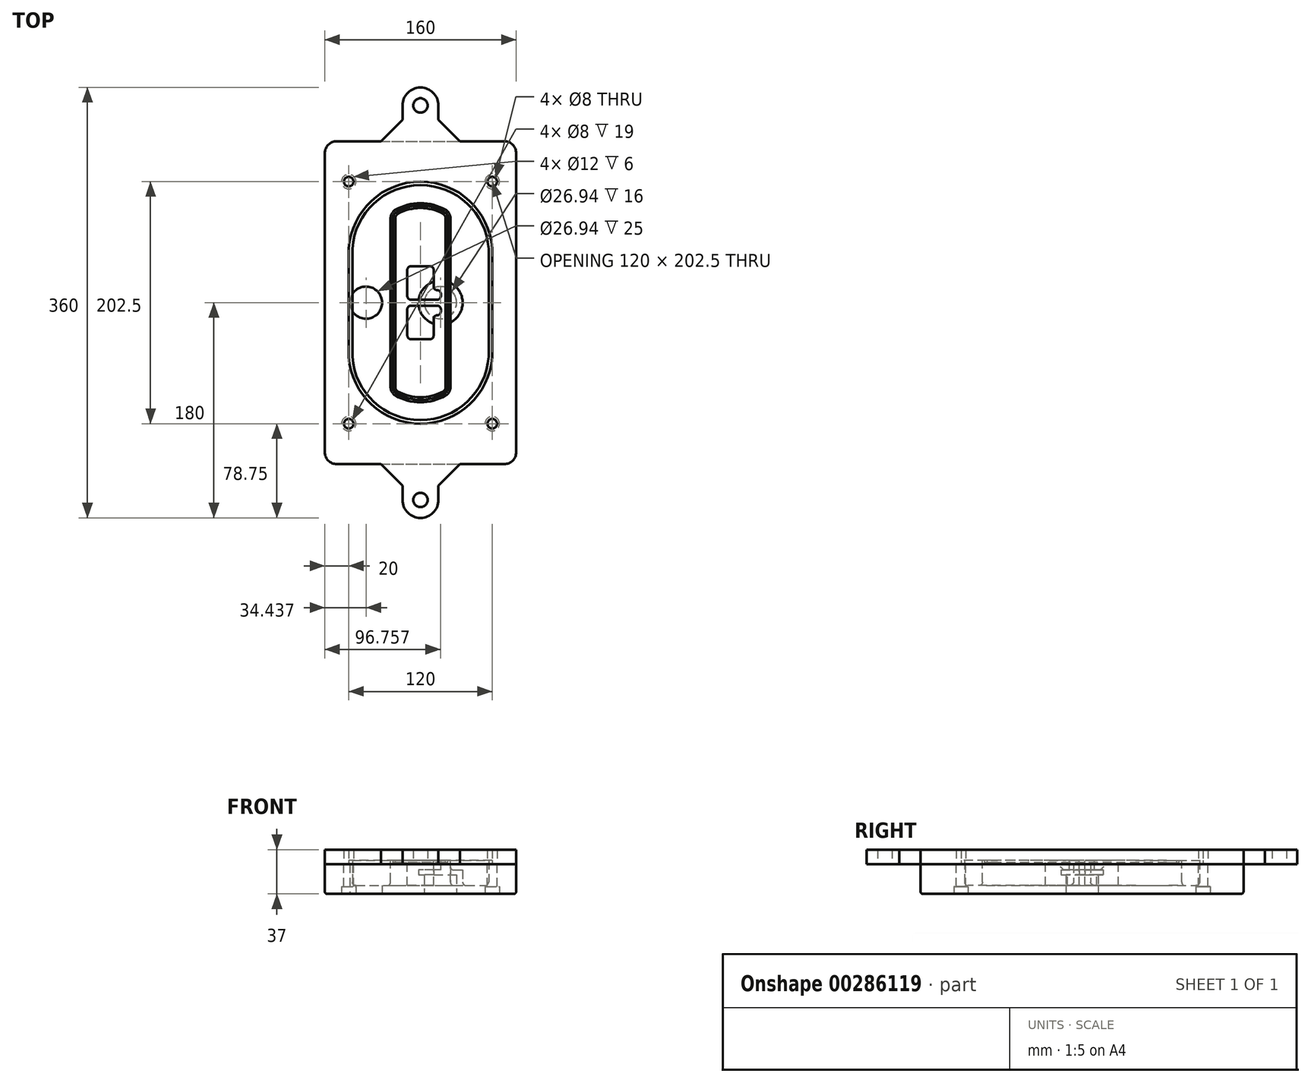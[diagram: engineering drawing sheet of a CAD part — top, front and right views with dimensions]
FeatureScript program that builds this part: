
annotation { "Feature Type Name" : "Feature", "Feature Type Description" : "" }
export const myFeature = defineFeature(function(context is Context, id is Id, definition is map)
    precondition{}
    {
        {
            var Q0;
            Q0=qCreatedBy(makeId("Top.planeOp"),FACE);
            var sketch = newSketch(context, id + "F0", { "sketchPlane" : qUnion([Q0])});
            skPoint(sketch, "E0.rect.middle", {"position": v(0, 0) * mm});
            skLineSegment(sketch, "E1.bottom", {"start": v(-70, -135) * mm, "end": v(70, -135) * mm});
            skLineSegment(sketch, "E1.top", {"start": v(-70, 135) * mm, "end": v(70, 135) * mm});
            skLineSegment(sketch, "E1.left", {"start": v(-80, -125) * mm, "end": v(-80, 125) * mm});
            skLineSegment(sketch, "E1.right", {"start": v(80, -125) * mm, "end": v(80, 125) * mm});
            skLineSegment(sketch, "E2", {"start": v(-80, 135) * mm, "end": v(80, -135) * mm, "construction": true});
            skLineSegment(sketch, "E3", {"start": v(80, 135) * mm, "end": v(-80, -135) * mm, "construction": true});
            skCircle(sketch, "E4", {"center": v(-60, 101.25) * mm, "radius": 4 * mm});
            skCircle(sketch, "E5", {"center": v(60, 101.25) * mm, "radius": 4 * mm});
            skCircle(sketch, "E6", {"center": v(60, -101.25) * mm, "radius": 4 * mm});
            skCircle(sketch, "E7", {"center": v(-60, -101.25) * mm, "radius": 4 * mm});
            skLineSegment(sketch, "E8", {"start": v(-60, 101.25) * mm, "end": v(60, 101.25) * mm, "construction": true});
            skLineSegment(sketch, "E9", {"start": v(60, 101.25) * mm, "end": v(60, -101.25) * mm, "construction": true});
            skLineSegment(sketch, "E10", {"start": v(60, -101.25) * mm, "end": v(-60, -101.25) * mm, "construction": true});
            skLineSegment(sketch, "E11", {"start": v(-60, -101.25) * mm, "end": v(-60, 101.25) * mm, "construction": true});
            skLineSegment(sketch, "E12", {"start": v(-60, 44.66) * mm, "end": v(-60, -44.66) * mm});
            skLineSegment(sketch, "E13", {"start": v(60, 44.66) * mm, "end": v(60, -44.66) * mm});
            skArc(sketch, "E14", {"start": v(59.98, 45.37) * mm, "mid": v(0, 101.25) * mm, "end": v(-59.98, 45.37) * mm});
            skArc(sketch, "E15", {"start": v(-59.98, -45.37) * mm, "mid": v(0, -101.25) * mm, "end": v(59.98, -45.37) * mm});
            skLineSegment(sketch, "E16", {"start": v(-60, 0) * mm, "end": v(60, 0) * mm, "construction": true});
            skPoint(sketch, "E17.visualSharp", {"position": v(-60, -45) * mm});
            skArc(sketch, "E17.filletArc", {"start": v(-60, -44.66) * mm, "mid": v(-60, -45.02) * mm, "end": v(-59.98, -45.37) * mm});
            skPoint(sketch, "E18.visualSharp", {"position": v(-60, 45) * mm});
            skArc(sketch, "E18.filletArc", {"start": v(-59.98, 45.37) * mm, "mid": v(-60, 45.02) * mm, "end": v(-60, 44.66) * mm});
            skPoint(sketch, "E19.visualSharp", {"position": v(60, 45) * mm});
            skArc(sketch, "E19.filletArc", {"start": v(60, 44.66) * mm, "mid": v(60, 45.02) * mm, "end": v(59.98, 45.37) * mm});
            skPoint(sketch, "E20.visualSharp", {"position": v(60, -45) * mm});
            skArc(sketch, "E20.filletArc", {"start": v(59.98, -45.37) * mm, "mid": v(60, -45.02) * mm, "end": v(60, -44.66) * mm});
            skPoint(sketch, "E21.visualSharp", {"position": v(-80, 135) * mm});
            skArc(sketch, "E21.filletArc", {"start": v(-70, 135) * mm, "mid": v(-77.07, 132.07) * mm, "end": v(-80, 125) * mm});
            skPoint(sketch, "E22.visualSharp", {"position": v(80, 135) * mm});
            skArc(sketch, "E22.filletArc", {"start": v(80, 125) * mm, "mid": v(77.07, 132.07) * mm, "end": v(70, 135) * mm});
            skPoint(sketch, "E23.visualSharp", {"position": v(80, -135) * mm});
            skArc(sketch, "E23.filletArc", {"start": v(70, -135) * mm, "mid": v(77.07, -132.07) * mm, "end": v(80, -125) * mm});
            skPoint(sketch, "E24.visualSharp", {"position": v(-80, -135) * mm});
            skArc(sketch, "E24.filletArc", {"start": v(-80, -125) * mm, "mid": v(-77.07, -132.07) * mm, "end": v(-70, -135) * mm});
            skArc(sketch, "E25.0", {"start": v(57, 44.66) * mm, "mid": v(57, 44.9) * mm, "end": v(56.98, 45.16) * mm});
            skLineSegment(sketch, "E25.1", {"start": v(57, 44.66) * mm, "end": v(57, -44.66) * mm});
            skArc(sketch, "E25.2", {"start": v(56.98, -45.16) * mm, "mid": v(57, -44.9) * mm, "end": v(57, -44.66) * mm});
            skArc(sketch, "E25.3", {"start": v(-56.98, -45.16) * mm, "mid": v(0, -98.25) * mm, "end": v(56.98, -45.16) * mm});
            skArc(sketch, "E25.4", {"start": v(-57, -44.66) * mm, "mid": v(-57, -44.9) * mm, "end": v(-56.98, -45.16) * mm});
            skArc(sketch, "E25.5", {"start": v(56.98, 45.16) * mm, "mid": v(0, 98.25) * mm, "end": v(-56.98, 45.16) * mm});
            skLineSegment(sketch, "E25.6", {"start": v(-57, 44.66) * mm, "end": v(-57, -44.66) * mm});
            skArc(sketch, "E25.7", {"start": v(-56.98, 45.16) * mm, "mid": v(-57, 44.9) * mm, "end": v(-57, 44.66) * mm});
            skArc(sketch, "E26.0", {"start": v(-63.97, 45.65) * mm, "mid": v(-64, 45.16) * mm, "end": v(-64, 44.66) * mm});
            skArc(sketch, "E26.1", {"start": v(63.97, 45.65) * mm, "mid": v(0, 105.25) * mm, "end": v(-63.97, 45.65) * mm});
            skArc(sketch, "E26.2", {"start": v(64, 44.66) * mm, "mid": v(64, 45.16) * mm, "end": v(63.97, 45.65) * mm});
            skLineSegment(sketch, "E26.3", {"start": v(64, 44.66) * mm, "end": v(64, -44.66) * mm});
            skArc(sketch, "E26.4", {"start": v(63.97, -45.65) * mm, "mid": v(64, -45.16) * mm, "end": v(64, -44.66) * mm});
            skLineSegment(sketch, "E26.5", {"start": v(-64, 44.66) * mm, "end": v(-64, -44.66) * mm});
            skArc(sketch, "E26.6", {"start": v(-63.97, -45.65) * mm, "mid": v(0, -105.25) * mm, "end": v(63.97, -45.65) * mm});
            skArc(sketch, "E26.7", {"start": v(-64, -44.66) * mm, "mid": v(-64, -45.16) * mm, "end": v(-63.97, -45.65) * mm});
            skSolve(sketch);
        }
        {
            var Q0;
            Q0=makeQuery(id+"F0.imprint","IMPRINT",FACE,{"disambiguationData":[TD([[makeQuery(id+"F0.imprint","IMPRINT",EDGE,{"derivedFrom":sQuery(id+"F0.wireOp",EDGE,"E1.bottom")}),1.0]])]});
            var Q1;
            Q1=makeQuery(id+"F0.imprint","IMPRINT",FACE,{"disambiguationData":[TD([[makeQuery(id+"F0.imprint","IMPRINT",EDGE,{"derivedFrom":sQuery(id+"F0.wireOp",EDGE,"E12")}),1.0]])]});
            var Q2;
            Q2=makeQuery(id+"F0.imprint","IMPRINT",FACE,{"disambiguationData":[TD([[makeQuery(id+"F0.imprint","IMPRINT",EDGE,{"derivedFrom":sQuery(id+"F0.wireOp",EDGE,"E25.0")}),1.0]])]});
            var Q3;
            Q3=makeQuery(id+"F0.imprint","IMPRINT",FACE,{"disambiguationData":[TD([[makeQuery(id+"F0.imprint","IMPRINT",EDGE,{"derivedFrom":sQuery(id+"F0.wireOp",EDGE,"E12")}),-1.0]])]});
            extrude(context, id + "F1", {"entities" : qUnion([Q0, Q1, Q2, Q3]), "oppositeDirection" : true, "depth" : 25 * mm});
        }
        {
            var Q0;
            Q0=makeQuery(id+"F0.imprint","IMPRINT",FACE,{"disambiguationData":[TD([[makeQuery(id+"F0.imprint","IMPRINT",EDGE,{"derivedFrom":sQuery(id+"F0.wireOp",EDGE,"E12")}),1.0]])]});
            extrude(context, id + "F2", {"entities" : qUnion([Q0]), "operationType" : NewBodyOperationType.ADD, "depth" : 3 * mm});
        }
        {
            var Q0;
            Q0=makeQuery(id+"F0.imprint","IMPRINT",FACE,{"disambiguationData":[TD([[makeQuery(id+"F0.imprint","IMPRINT",EDGE,{"derivedFrom":sQuery(id+"F0.wireOp",EDGE,"E25.0")}),1.0]])]});
            extrude(context, id + "F3", {"entities" : qUnion([Q0]), "operationType" : NewBodyOperationType.REMOVE, "oppositeDirection" : true, "depth" : 18 * mm});
        }
        {
            var Q0;
            Q0=makeQuery(id+"F2.opExtrude","CAP_FACE",FACE,{"disambiguationData":[OSD([sQuery(id+"F0.wireOp",EDGE,"E12"),sQuery(id+"F0.wireOp",EDGE,"E13"),sQuery(id+"F0.wireOp",EDGE,"E14"),sQuery(id+"F0.wireOp",EDGE,"E15"),sQuery(id+"F0.wireOp",EDGE,"E17.filletArc"),sQuery(id+"F0.wireOp",EDGE,"E18.filletArc"),sQuery(id+"F0.wireOp",EDGE,"E19.filletArc"),sQuery(id+"F0.wireOp",EDGE,"E20.filletArc"),sQuery(id+"F0.wireOp",EDGE,"E25.0"),sQuery(id+"F0.wireOp",EDGE,"E25.1"),sQuery(id+"F0.wireOp",EDGE,"E25.2"),sQuery(id+"F0.wireOp",EDGE,"E25.3"),sQuery(id+"F0.wireOp",EDGE,"E25.4"),sQuery(id+"F0.wireOp",EDGE,"E25.5"),sQuery(id+"F0.wireOp",EDGE,"E25.6"),sQuery(id+"F0.wireOp",EDGE,"E25.7")])],"isStart":false});
            var sketch = newSketch(context, id + "F4", { "sketchPlane" : qUnion([Q0])});
            skArc(sketch, "E27.0", {"start": v(-20.99, -77.65) * mm, "mid": v(0, -83.25) * mm, "end": v(20.99, -77.65) * mm});
            skArc(sketch, "E28.0", {"start": v(20.99, 77.65) * mm, "mid": v(0, 83.25) * mm, "end": v(-20.99, 77.65) * mm});
            skLineSegment(sketch, "E29", {"start": v(-25, 70.71) * mm, "end": v(-25, -70.71) * mm});
            skLineSegment(sketch, "E30", {"start": v(25, 70.71) * mm, "end": v(25, -70.71) * mm});
            skLineSegment(sketch, "E31", {"start": v(-25, 75.03) * mm, "end": v(25, 75.03) * mm, "construction": true});
            skLineSegment(sketch, "E32", {"start": v(-25, -75.03) * mm, "end": v(25, -75.03) * mm, "construction": true});
            skPoint(sketch, "E33.visualSharp", {"position": v(-25, 75.03) * mm});
            skArc(sketch, "E33.filletArc", {"start": v(-20.99, 77.65) * mm, "mid": v(-23.92, 74.72) * mm, "end": v(-25, 70.71) * mm});
            skPoint(sketch, "E34.visualSharp", {"position": v(25, 75.03) * mm});
            skArc(sketch, "E34.filletArc", {"start": v(25, 70.71) * mm, "mid": v(23.92, 74.72) * mm, "end": v(20.99, 77.65) * mm});
            skPoint(sketch, "E35.visualSharp", {"position": v(25, -75.03) * mm});
            skArc(sketch, "E35.filletArc", {"start": v(20.99, -77.65) * mm, "mid": v(23.92, -74.72) * mm, "end": v(25, -70.71) * mm});
            skPoint(sketch, "E36.visualSharp", {"position": v(-25, -75.03) * mm});
            skArc(sketch, "E36.filletArc", {"start": v(-25, -70.71) * mm, "mid": v(-23.92, -74.72) * mm, "end": v(-20.99, -77.65) * mm});
            skArc(sketch, "E37.0", {"start": v(56.98, 45.16) * mm, "mid": v(0, 98.25) * mm, "end": v(-56.98, 45.16) * mm});
            skArc(sketch, "E37.1", {"start": v(-56.98, 45.16) * mm, "mid": v(-57, 44.9) * mm, "end": v(-57, 44.66) * mm});
            skLineSegment(sketch, "E37.2", {"start": v(-57, 44.66) * mm, "end": v(-57, -44.66) * mm});
            skArc(sketch, "E37.3", {"start": v(-57, -44.66) * mm, "mid": v(-57, -44.9) * mm, "end": v(-56.98, -45.16) * mm});
            skArc(sketch, "E37.4", {"start": v(-56.98, -45.16) * mm, "mid": v(0, -98.25) * mm, "end": v(56.98, -45.16) * mm});
            skArc(sketch, "E37.5", {"start": v(56.98, -45.16) * mm, "mid": v(57, -44.9) * mm, "end": v(57, -44.66) * mm});
            skLineSegment(sketch, "E37.6", {"start": v(57, 44.66) * mm, "end": v(57, -44.66) * mm});
            skArc(sketch, "E37.7", {"start": v(57, 44.66) * mm, "mid": v(57, 44.9) * mm, "end": v(56.98, 45.16) * mm});
            skLineSegment(sketch, "E38.0", {"start": v(23, 70.71) * mm, "end": v(23, -70.71) * mm});
            skArc(sketch, "E38.1", {"start": v(19.99, -75.92) * mm, "mid": v(22.2, -73.72) * mm, "end": v(23, -70.71) * mm});
            skArc(sketch, "E38.2", {"start": v(-19.99, -75.92) * mm, "mid": v(0, -81.25) * mm, "end": v(19.99, -75.92) * mm});
            skArc(sketch, "E38.3", {"start": v(-23, -70.71) * mm, "mid": v(-22.2, -73.72) * mm, "end": v(-19.99, -75.92) * mm});
            skLineSegment(sketch, "E38.4", {"start": v(-23, 70.71) * mm, "end": v(-23, -70.71) * mm});
            skArc(sketch, "E38.5", {"start": v(23, 70.71) * mm, "mid": v(22.2, 73.72) * mm, "end": v(19.99, 75.92) * mm});
            skArc(sketch, "E38.6", {"start": v(-19.99, 75.92) * mm, "mid": v(-22.2, 73.72) * mm, "end": v(-23, 70.71) * mm});
            skArc(sketch, "E38.7", {"start": v(19.99, 75.92) * mm, "mid": v(0, 81.25) * mm, "end": v(-19.99, 75.92) * mm});
            skArc(sketch, "E39.0", {"start": v(21, 70.71) * mm, "mid": v(20.46, 72.72) * mm, "end": v(19, 74.18) * mm});
            skLineSegment(sketch, "E39.1", {"start": v(21, 70.71) * mm, "end": v(21, -70.71) * mm});
            skArc(sketch, "E39.2", {"start": v(19, -74.18) * mm, "mid": v(20.46, -72.72) * mm, "end": v(21, -70.71) * mm});
            skArc(sketch, "E39.3", {"start": v(-19, -74.18) * mm, "mid": v(0, -79.25) * mm, "end": v(19, -74.18) * mm});
            skArc(sketch, "E39.4", {"start": v(-21, -70.71) * mm, "mid": v(-20.46, -72.72) * mm, "end": v(-19, -74.18) * mm});
            skArc(sketch, "E39.5", {"start": v(19, 74.18) * mm, "mid": v(0, 79.25) * mm, "end": v(-19, 74.18) * mm});
            skLineSegment(sketch, "E39.6", {"start": v(-21, 70.71) * mm, "end": v(-21, -70.71) * mm});
            skArc(sketch, "E39.7", {"start": v(-19, 74.18) * mm, "mid": v(-20.46, 72.72) * mm, "end": v(-21, 70.71) * mm});
            skLineSegment(sketch, "E40", {"start": v(-25, 0) * mm, "end": v(25, 0) * mm, "construction": true});
            skLineSegment(sketch, "E41", {"start": v(-11, 5.5) * mm, "end": v(-11, 27.5) * mm});
            skLineSegment(sketch, "E42", {"start": v(-8, 30.5) * mm, "end": v(8, 30.5) * mm});
            skLineSegment(sketch, "E43", {"start": v(11, 27.5) * mm, "end": v(11, 13.5) * mm});
            skLineSegment(sketch, "E44", {"start": v(14, 10.5) * mm, "end": v(14, 10.5) * mm});
            skLineSegment(sketch, "E45", {"start": v(17, 7.5) * mm, "end": v(17, 5.5) * mm});
            skLineSegment(sketch, "E46", {"start": v(14, 2.5) * mm, "end": v(-8, 2.5) * mm});
            skPoint(sketch, "E47.visualSharp", {"position": v(-11, 30.5) * mm});
            skArc(sketch, "E47.filletArc", {"start": v(-8, 30.5) * mm, "mid": v(-10.12, 29.62) * mm, "end": v(-11, 27.5) * mm});
            skPoint(sketch, "E48.visualSharp", {"position": v(11, 30.5) * mm});
            skArc(sketch, "E48.filletArc", {"start": v(11, 27.5) * mm, "mid": v(10.12, 29.62) * mm, "end": v(8, 30.5) * mm});
            skPoint(sketch, "E49.visualSharp", {"position": v(11, 10.5) * mm});
            skArc(sketch, "E49.filletArc", {"start": v(11, 13.5) * mm, "mid": v(11.88, 11.38) * mm, "end": v(14, 10.5) * mm});
            skPoint(sketch, "E50.visualSharp", {"position": v(17, 10.5) * mm});
            skArc(sketch, "E50.filletArc", {"start": v(17, 7.5) * mm, "mid": v(16.12, 9.62) * mm, "end": v(14, 10.5) * mm});
            skPoint(sketch, "E51.visualSharp", {"position": v(17, 2.5) * mm});
            skArc(sketch, "E51.filletArc", {"start": v(14, 2.5) * mm, "mid": v(16.12, 3.38) * mm, "end": v(17, 5.5) * mm});
            skPoint(sketch, "E52.visualSharp", {"position": v(-11, 2.5) * mm});
            skArc(sketch, "E52.filletArc", {"start": v(-11, 5.5) * mm, "mid": v(-10.12, 3.38) * mm, "end": v(-8, 2.5) * mm});
            skLineSegment(sketch, "E53.0.MirrorCS", {"start": v(14, -2.5) * mm, "end": v(-8, -2.5) * mm});
            skArc(sketch, "E54.0.MirrorCS", {"start": v(-11, -5.5) * mm, "mid": v(-10.12, -3.38) * mm, "end": v(-8, -2.5) * mm});
            skLineSegment(sketch, "E55.0.MirrorCS", {"start": v(-11, -5.5) * mm, "end": v(-11, -27.5) * mm});
            skArc(sketch, "E56.0.MirrorCS", {"start": v(-8, -30.5) * mm, "mid": v(-10.12, -29.62) * mm, "end": v(-11, -27.5) * mm});
            skLineSegment(sketch, "E57.0.MirrorCS", {"start": v(-8, -30.5) * mm, "end": v(8, -30.5) * mm});
            skArc(sketch, "E58.0.MirrorCS", {"start": v(11, -27.5) * mm, "mid": v(10.12, -29.62) * mm, "end": v(8, -30.5) * mm});
            skLineSegment(sketch, "E59.0.MirrorCS", {"start": v(11, -27.5) * mm, "end": v(11, -13.5) * mm});
            skArc(sketch, "E60.0.MirrorCS", {"start": v(11, -13.5) * mm, "mid": v(11.88, -11.38) * mm, "end": v(14, -10.5) * mm});
            skArc(sketch, "E61.0.MirrorCS", {"start": v(17, -7.5) * mm, "mid": v(16.12, -9.62) * mm, "end": v(14, -10.5) * mm});
            skLineSegment(sketch, "E62.0.MirrorCS", {"start": v(17, -7.5) * mm, "end": v(17, -5.5) * mm});
            skArc(sketch, "E63.0.MirrorCS", {"start": v(14, -2.5) * mm, "mid": v(16.12, -3.38) * mm, "end": v(17, -5.5) * mm});
            skSolve(sketch);
        }
        {
            var Q0;
            Q0=makeQuery(id+"F4.imprint","IMPRINT",FACE,{"disambiguationData":[TD([[makeQuery(id+"F4.imprint","IMPRINT",EDGE,{"derivedFrom":sQuery(id+"F4.wireOp",EDGE,"E27.0")}),1.0]])]});
            var Q1;
            Q1=makeQuery(id+"F4.imprint","IMPRINT",FACE,{"disambiguationData":[TD([[makeQuery(id+"F4.imprint","IMPRINT",EDGE,{"derivedFrom":sQuery(id+"F4.wireOp",EDGE,"E38.0")}),-1.0]])]});
            var Q2;
            Q2=makeQuery(id+"F4.imprint","IMPRINT",FACE,{"disambiguationData":[TD([[makeQuery(id+"F4.imprint","IMPRINT",EDGE,{"derivedFrom":sQuery(id+"F4.wireOp",EDGE,"E39.0")}),1.0]])]});
            extrude(context, id + "F5", {"entities" : qUnion([Q0, Q1, Q2]), "operationType" : NewBodyOperationType.ADD, "endBound" : BoundingType.UP_TO_NEXT, "oppositeDirection" : true, "depth" : 25 * mm});
        }
        {
            var Q0;
            Q0=makeQuery(id+"F4.imprint","IMPRINT",FACE,{"disambiguationData":[TD([[makeQuery(id+"F4.imprint","IMPRINT",EDGE,{"derivedFrom":sQuery(id+"F4.wireOp",EDGE,"E38.0")}),-1.0]])]});
            extrude(context, id + "F6", {"entities" : qUnion([Q0]), "operationType" : NewBodyOperationType.REMOVE, "oppositeDirection" : true, "depth" : 2 * mm});
        }
        {
            var Q0;
            Q0=makeQuery(id+"F1.opExtrude","CAP_FACE",FACE,{"disambiguationData":[OSD([sQuery(id+"F0.wireOp",EDGE,"E1.bottom"),sQuery(id+"F0.wireOp",EDGE,"E1.top"),sQuery(id+"F0.wireOp",EDGE,"E1.left"),sQuery(id+"F0.wireOp",EDGE,"E1.right"),sQuery(id+"F0.wireOp",EDGE,"E4"),sQuery(id+"F0.wireOp",EDGE,"E5"),sQuery(id+"F0.wireOp",EDGE,"E6"),sQuery(id+"F0.wireOp",EDGE,"E7"),sQuery(id+"F0.wireOp",EDGE,"E21.filletArc"),sQuery(id+"F0.wireOp",EDGE,"E22.filletArc"),sQuery(id+"F0.wireOp",EDGE,"E23.filletArc"),sQuery(id+"F0.wireOp",EDGE,"E24.filletArc")])],"isStart":false});
            var sketch = newSketch(context, id + "F7", { "sketchPlane" : qUnion([Q0])});
            skCircle(sketch, "E64", {"center": v(16.76, 0) * mm, "radius": 13.47 * mm});
            skCircle(sketch, "E65", {"center": v(-45.56, 0) * mm, "radius": 13.47 * mm});
            skLineSegment(sketch, "E66", {"start": v(80, 0) * mm, "end": v(-80, 0) * mm});
            skCircle(sketch, "E67", {"center": v(16.76, 0) * mm, "radius": 18.47 * mm});
            skCircle(sketch, "E68", {"center": v(60, -101.25) * mm, "radius": 6 * mm});
            skCircle(sketch, "E69", {"center": v(-60, -101.25) * mm, "radius": 6 * mm});
            skCircle(sketch, "E70", {"center": v(-60, 101.25) * mm, "radius": 6 * mm});
            skCircle(sketch, "E71", {"center": v(60, 101.25) * mm, "radius": 6 * mm});
            skSolve(sketch);
        }
        {
            var Q0;
            {var subQ1=sQuery(id+"F7.wireOp",EDGE,"E66");var subQ4=sQuery(id+"F7.wireOp",EDGE,"E64");var subQ6=makeQuery(id+"F7.imprint","INTERSECT",VERTEX,{"disambiguationData":[OD(0.0)],"derivedFrom":[subQ4,subQ1]});Q0=makeQuery(id+"F7.imprint","IMPRINT",FACE,{"disambiguationData":[TD([[makeQuery(id+"F7.imprint","IMPRINT",EDGE,{"disambiguationData":[TD([[subQ6,-1.0]])],"derivedFrom":subQ4}),-1.0]])]});}
            var Q1;
            {var subQ0=sQuery(id+"F7.wireOp",EDGE,"E66");var subQ1=sQuery(id+"F7.wireOp",EDGE,"E64");var subQ3=makeQuery(id+"F7.imprint","INTERSECT",VERTEX,{"disambiguationData":[OD(0.0)],"derivedFrom":[subQ1,subQ0]});Q1=makeQuery(id+"F7.imprint","IMPRINT",FACE,{"disambiguationData":[TD([[makeQuery(id+"F7.imprint","IMPRINT",EDGE,{"disambiguationData":[TD([[subQ3,-1.0]])],"derivedFrom":subQ1}),1.0]])]});}
            var Q2;
            {var subQ0=sQuery(id+"F7.wireOp",EDGE,"E66");var subQ1=sQuery(id+"F7.wireOp",EDGE,"E64");var subQ3=makeQuery(id+"F7.imprint","INTERSECT",VERTEX,{"disambiguationData":[OD(0.0)],"derivedFrom":[subQ1,subQ0]});Q2=makeQuery(id+"F7.imprint","IMPRINT",FACE,{"disambiguationData":[TD([[makeQuery(id+"F7.imprint","IMPRINT",EDGE,{"disambiguationData":[TD([[subQ3,1.0]])],"derivedFrom":subQ1}),1.0]])]});}
            var Q3;
            {var subQ1=sQuery(id+"F7.wireOp",EDGE,"E66");var subQ4=sQuery(id+"F7.wireOp",EDGE,"E64");var subQ6=makeQuery(id+"F7.imprint","INTERSECT",VERTEX,{"disambiguationData":[OD(0.0)],"derivedFrom":[subQ4,subQ1]});Q3=makeQuery(id+"F7.imprint","IMPRINT",FACE,{"disambiguationData":[TD([[makeQuery(id+"F7.imprint","IMPRINT",EDGE,{"disambiguationData":[TD([[subQ6,1.0]])],"derivedFrom":subQ4}),-1.0]])]});}
            extrude(context, id + "F8", {"entities" : qUnion([Q0, Q1, Q2, Q3]), "operationType" : NewBodyOperationType.ADD, "oppositeDirection" : true, "depth" : 20 * mm});
        }
        {
            var Q0;
            {var subQ0=sQuery(id+"F7.wireOp",EDGE,"E66");var subQ1=sQuery(id+"F7.wireOp",EDGE,"E64");var subQ3=makeQuery(id+"F7.imprint","INTERSECT",VERTEX,{"disambiguationData":[OD(0.0)],"derivedFrom":[subQ1,subQ0]});Q0=makeQuery(id+"F7.imprint","IMPRINT",FACE,{"disambiguationData":[TD([[makeQuery(id+"F7.imprint","IMPRINT",EDGE,{"disambiguationData":[TD([[subQ3,-1.0]])],"derivedFrom":subQ1}),1.0]])]});}
            var Q1;
            {var subQ0=sQuery(id+"F7.wireOp",EDGE,"E66");var subQ1=sQuery(id+"F7.wireOp",EDGE,"E64");var subQ3=makeQuery(id+"F7.imprint","INTERSECT",VERTEX,{"disambiguationData":[OD(0.0)],"derivedFrom":[subQ1,subQ0]});Q1=makeQuery(id+"F7.imprint","IMPRINT",FACE,{"disambiguationData":[TD([[makeQuery(id+"F7.imprint","IMPRINT",EDGE,{"disambiguationData":[TD([[subQ3,1.0]])],"derivedFrom":subQ1}),1.0]])]});}
            extrude(context, id + "F9", {"entities" : qUnion([Q0, Q1]), "operationType" : NewBodyOperationType.REMOVE, "oppositeDirection" : true, "depth" : 16 * mm});
        }
        {
            var Q0;
            {var subQ0=sQuery(id+"F7.wireOp",EDGE,"E66");var subQ1=sQuery(id+"F7.wireOp",EDGE,"E65");var subQ3=makeQuery(id+"F7.imprint","INTERSECT",VERTEX,{"disambiguationData":[OD(0.0)],"derivedFrom":[subQ1,subQ0]});Q0=makeQuery(id+"F7.imprint","IMPRINT",FACE,{"disambiguationData":[TD([[makeQuery(id+"F7.imprint","IMPRINT",EDGE,{"disambiguationData":[TD([[subQ3,-1.0]])],"derivedFrom":subQ1}),1.0]])]});}
            var Q1;
            {var subQ0=sQuery(id+"F7.wireOp",EDGE,"E66");var subQ1=sQuery(id+"F7.wireOp",EDGE,"E65");var subQ3=makeQuery(id+"F7.imprint","INTERSECT",VERTEX,{"disambiguationData":[OD(0.0)],"derivedFrom":[subQ1,subQ0]});Q1=makeQuery(id+"F7.imprint","IMPRINT",FACE,{"disambiguationData":[TD([[makeQuery(id+"F7.imprint","IMPRINT",EDGE,{"disambiguationData":[TD([[subQ3,1.0]])],"derivedFrom":subQ1}),1.0]])]});}
            extrude(context, id + "F10", {"entities" : qUnion([Q0, Q1]), "operationType" : NewBodyOperationType.REMOVE, "oppositeDirection" : true, "depth" : 25 * mm});
        }
        {
            var Q0;
            Q0=makeQuery(id+"F7.imprint","IMPRINT",FACE,{"disambiguationData":[TD([[makeQuery(id+"F7.imprint","IMPRINT",EDGE,{"derivedFrom":sQuery(id+"F7.wireOp",EDGE,"E68")}),1.0]])]});
            var Q1;
            Q1=makeQuery(id+"F7.imprint","IMPRINT",FACE,{"disambiguationData":[TD([[makeQuery(id+"F7.imprint","IMPRINT",EDGE,{"derivedFrom":makeQuery(id+"F1.opExtrude","CAP_EDGE",EDGE,{"disambiguationData":[OSD([sQuery(id+"F0.wireOp",EDGE,"E5")])],"isStart":false})}),-1.0]])]});
            var Q2;
            Q2=makeQuery(id+"F7.imprint","IMPRINT",FACE,{"disambiguationData":[TD([[makeQuery(id+"F7.imprint","IMPRINT",EDGE,{"derivedFrom":sQuery(id+"F7.wireOp",EDGE,"E69")}),1.0]])]});
            var Q3;
            Q3=makeQuery(id+"F7.imprint","IMPRINT",FACE,{"disambiguationData":[TD([[makeQuery(id+"F7.imprint","IMPRINT",EDGE,{"derivedFrom":makeQuery(id+"F1.opExtrude","CAP_EDGE",EDGE,{"disambiguationData":[OSD([sQuery(id+"F0.wireOp",EDGE,"E4")])],"isStart":false})}),-1.0]])]});
            var Q4;
            Q4=makeQuery(id+"F7.imprint","IMPRINT",FACE,{"disambiguationData":[TD([[makeQuery(id+"F7.imprint","IMPRINT",EDGE,{"derivedFrom":sQuery(id+"F7.wireOp",EDGE,"E70")}),1.0]])]});
            var Q5;
            Q5=makeQuery(id+"F7.imprint","IMPRINT",FACE,{"disambiguationData":[TD([[makeQuery(id+"F7.imprint","IMPRINT",EDGE,{"derivedFrom":makeQuery(id+"F1.opExtrude","CAP_EDGE",EDGE,{"disambiguationData":[OSD([sQuery(id+"F0.wireOp",EDGE,"E7")])],"isStart":false})}),-1.0]])]});
            var Q6;
            Q6=makeQuery(id+"F7.imprint","IMPRINT",FACE,{"disambiguationData":[TD([[makeQuery(id+"F7.imprint","IMPRINT",EDGE,{"derivedFrom":sQuery(id+"F7.wireOp",EDGE,"E71")}),1.0]])]});
            var Q7;
            Q7=makeQuery(id+"F7.imprint","IMPRINT",FACE,{"disambiguationData":[TD([[makeQuery(id+"F7.imprint","IMPRINT",EDGE,{"derivedFrom":makeQuery(id+"F1.opExtrude","CAP_EDGE",EDGE,{"disambiguationData":[OSD([sQuery(id+"F0.wireOp",EDGE,"E6")])],"isStart":false})}),-1.0]])]});
            extrude(context, id + "F11", {"entities" : qUnion([Q0, Q1, Q2, Q3, Q4, Q5, Q6, Q7]), "operationType" : NewBodyOperationType.REMOVE, "oppositeDirection" : true, "depth" : 6 * mm});
        }
        {
            var Q0;
            Q0=makeQuery(id+"F9.boolean.opBoolean","COPY",FACE,{"derivedFrom":makeQuery(id+"F9.opExtrude","CAP_FACE",FACE,{"disambiguationData":[OSD([sQuery(id+"F7.wireOp",EDGE,"E64")])],"isStart":false})});
            var sketch = newSketch(context, id + "F12", { "sketchPlane" : qUnion([Q0])});
            skArc(sketch, "E72.0", {"start": v(11, 17.55) * mm, "mid": v(2.57, 11.82) * mm, "end": v(-1.54, 2.5) * mm});
            skArc(sketch, "E72.1", {"start": v(-1.54, -2.5) * mm, "mid": v(2.57, -11.82) * mm, "end": v(11, -17.55) * mm});
            skLineSegment(sketch, "E73", {"start": v(-1.54, -2.5) * mm, "end": v(14, -2.5) * mm});
            skLineSegment(sketch, "E74.0", {"start": v(14, 2.5) * mm, "end": v(-1.54, 2.5) * mm});
            skArc(sketch, "E74.1", {"start": v(14, 2.5) * mm, "mid": v(16.12, 3.38) * mm, "end": v(17, 5.5) * mm});
            skLineSegment(sketch, "E74.2", {"start": v(17, 7.5) * mm, "end": v(17, 5.5) * mm});
            skArc(sketch, "E74.3", {"start": v(17, 7.5) * mm, "mid": v(16.12, 9.62) * mm, "end": v(14, 10.5) * mm});
            skArc(sketch, "E74.4", {"start": v(11, 13.5) * mm, "mid": v(11.88, 11.38) * mm, "end": v(14, 10.5) * mm});
            skLineSegment(sketch, "E74.5", {"start": v(11, 17.55) * mm, "end": v(11, 13.5) * mm});
            skLineSegment(sketch, "E74.7", {"start": v(14, -2.5) * mm, "end": v(-1.54, -2.5) * mm});
            skArc(sketch, "E74.8", {"start": v(14, -2.5) * mm, "mid": v(16.12, -3.38) * mm, "end": v(17, -5.5) * mm});
            skLineSegment(sketch, "E74.9", {"start": v(17, -7.5) * mm, "end": v(17, -5.5) * mm});
            skArc(sketch, "E74.10", {"start": v(17, -7.5) * mm, "mid": v(16.12, -9.62) * mm, "end": v(14, -10.5) * mm});
            skArc(sketch, "E74.11", {"start": v(11, -13.5) * mm, "mid": v(11.88, -11.38) * mm, "end": v(14, -10.5) * mm});
            skLineSegment(sketch, "E74.12", {"start": v(11, -17.55) * mm, "end": v(11, -13.5) * mm});
            skPoint(sketch, "E75.orphan", {"position": v(11, -27.5) * mm});
            skPoint(sketch, "E76.orphan", {"position": v(-8, -2.5) * mm});
            skPoint(sketch, "E77.orphan", {"position": v(-8, 2.5) * mm});
            skPoint(sketch, "E78.orphan", {"position": v(11, 27.5) * mm});
            skSolve(sketch);
        }
        {
            var Q0;
            {var subQ7=sQuery(id+"F12.wireOp",EDGE,"E72.0");var subQ14=sQuery(id+"F12.wireOp",EDGE,"E72.1");var subQ16=sQuery(id+"F12.wireOp",EDGE,"E74.1");var subQ18=sQuery(id+"F12.wireOp",EDGE,"E74.8");Q0=qUnion([makeQuery(id+"F12.imprint","IMPRINT",FACE,{"disambiguationData":[TD([[makeQuery(id+"F12.imprint","IMPRINT",EDGE,{"derivedFrom":subQ7}),1.0]])]}),makeQuery(id+"F12.imprint","IMPRINT",FACE,{"disambiguationData":[TD([[makeQuery(id+"F12.imprint","IMPRINT",EDGE,{"derivedFrom":subQ14}),1.0]])]}),makeQuery(id+"F12.imprint","IMPRINT",FACE,{"disambiguationData":[TD([[makeQuery(id+"F12.imprint","IMPRINT",EDGE,{"derivedFrom":subQ16}),1.0]])]}),makeQuery(id+"F12.imprint","IMPRINT",FACE,{"disambiguationData":[TD([[makeQuery(id+"F12.imprint","IMPRINT",EDGE,{"derivedFrom":subQ18}),-1.0]])]})]);}
            var Q1;
            Q1=makeQuery(id+"F5.boolean.opBoolean","SPLIT",FACE,{"disambiguationData":[TD([makeQuery(id+"F5.opExtrude","SWEPT_FACE",FACE,{"disambiguationData":[OSD([sQuery(id+"F4.wireOp",EDGE,"E41")])]})])],"derivedFrom":makeQuery(id+"F3.boolean.opBoolean","COPY",FACE,{"derivedFrom":makeQuery(id+"F3.opExtrude","CAP_FACE",FACE,{"disambiguationData":[OSD([sQuery(id+"F0.wireOp",EDGE,"E25.0"),sQuery(id+"F0.wireOp",EDGE,"E25.1"),sQuery(id+"F0.wireOp",EDGE,"E25.2"),sQuery(id+"F0.wireOp",EDGE,"E25.3"),sQuery(id+"F0.wireOp",EDGE,"E25.4"),sQuery(id+"F0.wireOp",EDGE,"E25.5"),sQuery(id+"F0.wireOp",EDGE,"E25.6"),sQuery(id+"F0.wireOp",EDGE,"E25.7")])],"isStart":false})})});
            extrude(context, id + "F13", {"entities" : qUnion([Q0]), "operationType" : NewBodyOperationType.REMOVE, "endBound" : BoundingType.UP_TO_SURFACE, "endBoundEntityFace" : qUnion([Q1]), "depth" : 25 * mm});
        }
        {
            var Q0;
            Q0=makeQuery(id+"F3.boolean.opBoolean","COPY",EDGE,{"derivedFrom":makeQuery(id+"F3.opExtrude","CAP_EDGE",EDGE,{"disambiguationData":[OSD([sQuery(id+"F0.wireOp",EDGE,"E25.6")])],"isStart":false})});
            var Q1;
            Q1=makeQuery(id+"F8.boolean.opBoolean","INTERSECT",EDGE,{"derivedFrom":[makeQuery(id+"F5.opExtrude","SWEPT_FACE",FACE,{"disambiguationData":[OSD([sQuery(id+"F4.wireOp",EDGE,"E30")])]}),makeQuery(id+"F8.opExtrude","CAP_FACE",FACE,{"disambiguationData":[OSD([sQuery(id+"F7.wireOp",EDGE,"E67")])],"isStart":false})]});
            var Q2;
            Q2=makeQuery(id+"F8.boolean.opBoolean","INTERSECT",EDGE,{"disambiguationData":[OD(1.0)],"derivedFrom":[makeQuery(id+"F5.opExtrude","SWEPT_FACE",FACE,{"disambiguationData":[OSD([sQuery(id+"F4.wireOp",EDGE,"E30")])]}),makeQuery(id+"F8.opExtrude","SWEPT_FACE",FACE,{"disambiguationData":[OSD([sQuery(id+"F7.wireOp",EDGE,"E67")])]})]});
            var Q3;
            {var subQ0=sQuery(id+"F4.wireOp",EDGE,"E30");Q3=makeQuery(id+"F8.boolean.opBoolean","SPLIT",EDGE,{"disambiguationData":[TD([makeQuery(id+"F5.opExtrude","SWEPT_FACE",FACE,{"disambiguationData":[OSD([sQuery(id+"F4.wireOp",EDGE,"E35.filletArc")])]})])],"derivedFrom":makeQuery(id+"F5.opExtrude","CAP_EDGE",EDGE,{"disambiguationData":[OSD([subQ0])],"isStart":false})});}
            var Q4;
            {var subQ0=sQuery(id+"F0.wireOp",EDGE,"E25.7");var subQ1=sQuery(id+"F0.wireOp",EDGE,"E25.1");var subQ2=sQuery(id+"F0.wireOp",EDGE,"E25.6");var subQ3=sQuery(id+"F0.wireOp",EDGE,"E25.5");var subQ4=sQuery(id+"F0.wireOp",EDGE,"E25.4");var subQ5=sQuery(id+"F0.wireOp",EDGE,"E25.0");var subQ6=sQuery(id+"F0.wireOp",EDGE,"E25.2");var subQ7=sQuery(id+"F0.wireOp",EDGE,"E25.3");Q4=makeQuery(id+"F8.boolean.opBoolean","INTERSECT",EDGE,{"derivedFrom":[makeQuery(id+"F5.boolean.opBoolean","SPLIT",FACE,{"disambiguationData":[TD([makeQuery(id+"F2.opExtrude","SWEPT_FACE",FACE,{"disambiguationData":[OSD([subQ5])]})])],"derivedFrom":makeQuery(id+"F3.boolean.opBoolean","COPY",FACE,{"derivedFrom":makeQuery(id+"F3.opExtrude","CAP_FACE",FACE,{"disambiguationData":[OSD([subQ5,subQ1,subQ6,subQ7,subQ4,subQ3,subQ2,subQ0])],"isStart":false})})}),makeQuery(id+"F8.opExtrude","SWEPT_FACE",FACE,{"disambiguationData":[OSD([sQuery(id+"F7.wireOp",EDGE,"E67")])]})]});}
            var Q5;
            Q5=makeQuery(id+"F8.boolean.opBoolean","INTERSECT",EDGE,{"disambiguationData":[OD(0.0)],"derivedFrom":[makeQuery(id+"F5.opExtrude","SWEPT_FACE",FACE,{"disambiguationData":[OSD([sQuery(id+"F4.wireOp",EDGE,"E30")])]}),makeQuery(id+"F8.opExtrude","SWEPT_FACE",FACE,{"disambiguationData":[OSD([sQuery(id+"F7.wireOp",EDGE,"E67")])]})]});
            fillet(context, id + "F14", {"entities" : qUnion([Q0, Q1, Q2, Q3, Q4, Q5]), "radius" : 3 * mm, "tangentPropagation" : true, "allowEdgeOverflow" : false});
        }
        {
            var Q0;
            Q0=makeQuery(id+"F1.opExtrude","CAP_EDGE",EDGE,{"disambiguationData":[OSD([sQuery(id+"F0.wireOp",EDGE,"E1.bottom")])],"isStart":false});
            fillet(context, id + "F15", {"entities" : qUnion([Q0]), "radius" : 2 * mm, "tangentPropagation" : true, "allowEdgeOverflow" : false});
        }
        {
            var Q0;
            {var subQ0=sQuery(id+"F0.wireOp",EDGE,"E21.filletArc");var subQ1=sQuery(id+"F0.wireOp",EDGE,"E7");var subQ2=sQuery(id+"F0.wireOp",EDGE,"E6");var subQ3=sQuery(id+"F0.wireOp",EDGE,"E5");var subQ4=sQuery(id+"F0.wireOp",EDGE,"E4");var subQ5=sQuery(id+"F0.wireOp",EDGE,"E22.filletArc");var subQ6=sQuery(id+"F0.wireOp",EDGE,"E1.bottom");var subQ7=sQuery(id+"F0.wireOp",EDGE,"E1.right");var subQ8=sQuery(id+"F0.wireOp",EDGE,"E1.top");var subQ9=sQuery(id+"F0.wireOp",EDGE,"E1.left");var subQ10=sQuery(id+"F0.wireOp",EDGE,"E23.filletArc");var subQ11=sQuery(id+"F0.wireOp",EDGE,"E24.filletArc");Q0=makeQuery(id+"F2.boolean.opBoolean","SPLIT",FACE,{"disambiguationData":[TD([makeQuery(id+"F1.opExtrude","SWEPT_FACE",FACE,{"disambiguationData":[OSD([subQ6])]})])],"derivedFrom":makeQuery(id+"F1.opExtrude","CAP_FACE",FACE,{"disambiguationData":[OSD([subQ6,subQ8,subQ9,subQ7,subQ4,subQ3,subQ2,subQ1,subQ0,subQ5,subQ10,subQ11])],"isStart":true})});}
            var sketch = newSketch(context, id + "F16", { "sketchPlane" : qUnion([Q0])});
            skCircle(sketch, "E79", {"center": v(0, 165) * mm, "radius": 6 * mm});
            skArc(sketch, "E80", {"start": v(15, 165) * mm, "mid": v(0, 180) * mm, "end": v(-15, 165) * mm});
            skLineSegment(sketch, "E81", {"start": v(-15, 165) * mm, "end": v(-15, 153) * mm});
            skLineSegment(sketch, "E82", {"start": v(-15, 153) * mm, "end": v(-33, 135) * mm});
            skPoint(sketch, "E83.1", {"position": v(70, 135) * mm});
            skArc(sketch, "E83.2", {"start": v(80, 125) * mm, "mid": v(77.07, 132.07) * mm, "end": v(70, 135) * mm});
            skLineSegment(sketch, "E83.3", {"start": v(80, -125) * mm, "end": v(80, 125) * mm});
            skArc(sketch, "E83.4", {"start": v(-70, 135) * mm, "mid": v(-77.07, 132.07) * mm, "end": v(-80, 125) * mm});
            skLineSegment(sketch, "E83.5", {"start": v(-80, -125) * mm, "end": v(-80, 125) * mm});
            skCircle(sketch, "E83.6", {"center": v(-60, 101.25) * mm, "radius": 4 * mm});
            skPoint(sketch, "E83.8", {"position": v(77.07, 132.07) * mm});
            skLineSegment(sketch, "E84", {"start": v(15, 165) * mm, "end": v(15, 153) * mm});
            skLineSegment(sketch, "E85", {"start": v(15, 153) * mm, "end": v(33, 135) * mm});
            skLineSegment(sketch, "E86", {"start": v(80, 0) * mm, "end": v(-80, 0) * mm, "construction": true});
            skLineSegment(sketch, "E87.MirrorCS", {"start": v(-15, -153) * mm, "end": v(-33, -135) * mm});
            skCircle(sketch, "E88.MirrorC", {"center": v(0, -165) * mm, "radius": 6 * mm});
            skArc(sketch, "E89.MirrorCS", {"start": v(15, -165) * mm, "mid": v(0, -180) * mm, "end": v(-15, -165) * mm});
            skLineSegment(sketch, "E90.MirrorCS", {"start": v(-15, -165) * mm, "end": v(-15, -153) * mm});
            skLineSegment(sketch, "E91.MirrorCS", {"start": v(15, -165) * mm, "end": v(15, -153) * mm});
            skLineSegment(sketch, "E92.MirrorCS", {"start": v(15, -153) * mm, "end": v(33, -135) * mm});
            skPoint(sketch, "E93", {"position": v(0, 135) * mm});
            skLineSegment(sketch, "E94", {"start": v(0, 165) * mm, "end": v(0, 135) * mm, "construction": true});
            skSolve(sketch);
        }
        {
            var Q0;
            Q0=makeQuery(id+"F16.imprint","IMPRINT",FACE,{"disambiguationData":[TD([[makeQuery(id+"F16.imprint","IMPRINT",EDGE,{"derivedFrom":sQuery(id+"F16.wireOp",EDGE,"E79")}),-1.0]])]});
            var Q1;
            {var subQ0=sQuery(id+"F16.wireOp",EDGE,"E87.MirrorCS");Q1=makeQuery(id+"F16.imprint","IMPRINT",FACE,{"disambiguationData":[TD([[makeQuery(id+"F16.imprint","IMPRINT",EDGE,{"derivedFrom":subQ0}),-1.0]])]});}
            var Q2;
            {var subQ7=sQuery(id+"F16.wireOp",EDGE,"E83.2");Q2=makeQuery(id+"F16.imprint","IMPRINT",FACE,{"disambiguationData":[TD([[makeQuery(id+"F16.imprint","IMPRINT",EDGE,{"derivedFrom":subQ7}),1.0]])]});}
            extrude(context, id + "F17", {"entities" : qUnion([Q0, Q1, Q2]), "depth" : 12 * mm});
        }
    });
